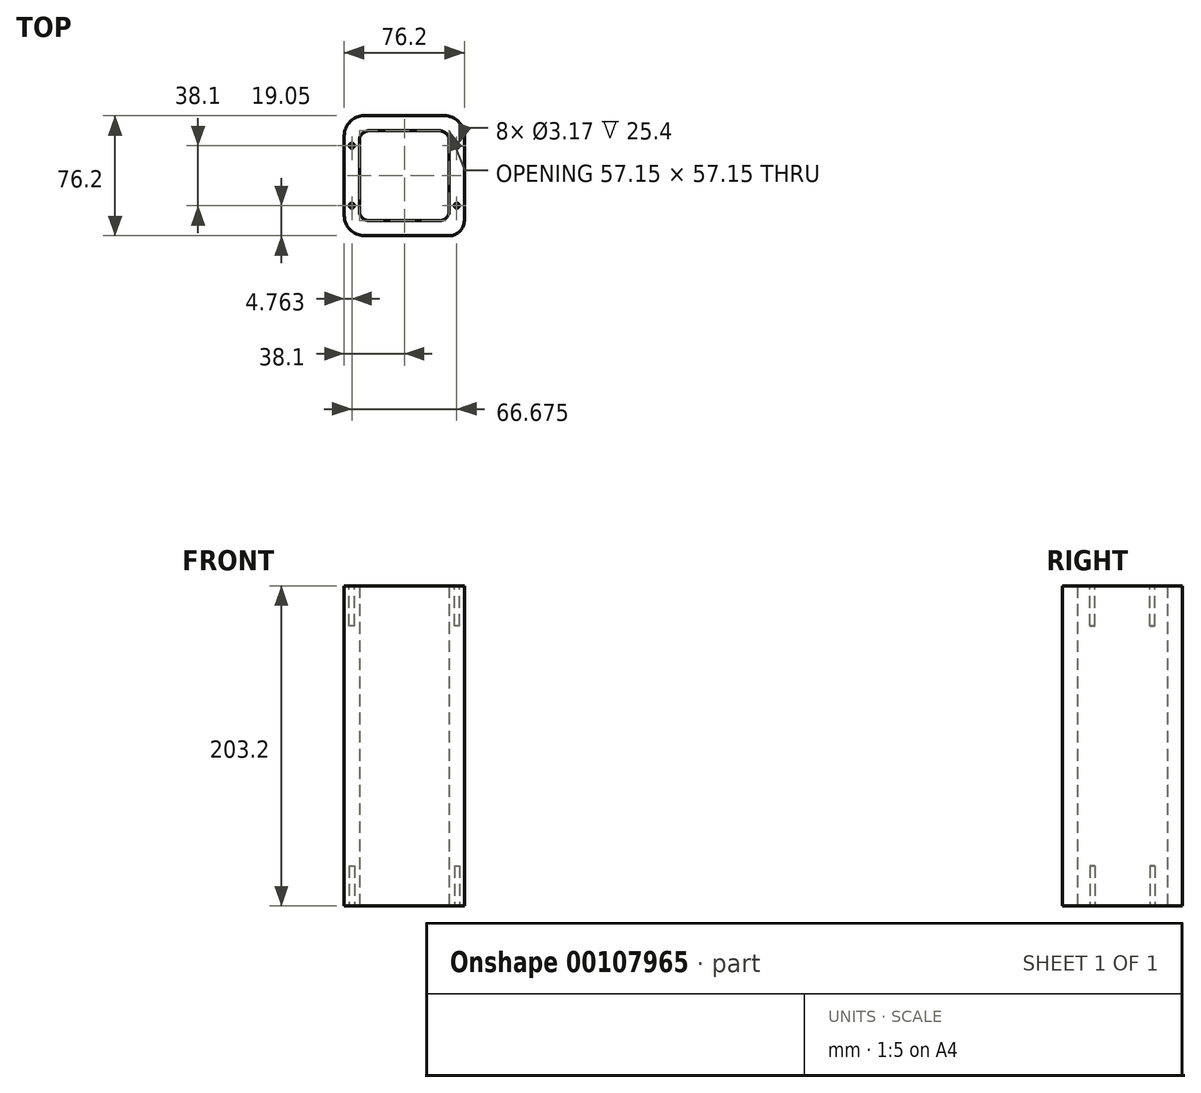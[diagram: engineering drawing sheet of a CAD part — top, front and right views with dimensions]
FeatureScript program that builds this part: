
annotation { "Feature Type Name" : "Feature", "Feature Type Description" : "" }
export const myFeature = defineFeature(function(context is Context, id is Id, definition is map)
    precondition{}
    {
        {
            var Q0;
            Q0=qCreatedBy(makeId("Top.planeOp"),FACE);
            var sketch = newSketch(context, id + "F0", { "sketchPlane" : qUnion([Q0])});
            skLineSegment(sketch, "E0.bottom", {"start": v(28.57, -38.1) * mm, "end": v(-25.4, -38.1) * mm});
            skLineSegment(sketch, "E0.top", {"start": v(25.4, 38.1) * mm, "end": v(-25.4, 38.1) * mm});
            skLineSegment(sketch, "E0.left", {"start": v(38.1, -28.58) * mm, "end": v(38.1, 25.4) * mm});
            skLineSegment(sketch, "E0.right", {"start": v(-38.1, -25.4) * mm, "end": v(-38.1, 25.4) * mm});
            skPoint(sketch, "E0.middle", {"position": v(0, 0) * mm});
            skPoint(sketch, "E1.visualSharp", {"position": v(-38.1, 38.1) * mm});
            skArc(sketch, "E1.filletArc", {"start": v(-25.4, 38.1) * mm, "mid": v(-34.38, 34.38) * mm, "end": v(-38.1, 25.4) * mm});
            skPoint(sketch, "E2.visualSharp", {"position": v(38.1, 38.1) * mm});
            skArc(sketch, "E2.filletArc", {"start": v(38.1, 25.4) * mm, "mid": v(34.38, 34.38) * mm, "end": v(25.4, 38.1) * mm});
            skPoint(sketch, "E3.visualSharp", {"position": v(38.1, -38.1) * mm});
            skArc(sketch, "E3.filletArc", {"start": v(28.58, -38.1) * mm, "mid": v(35.31, -35.31) * mm, "end": v(38.1, -28.58) * mm});
            skPoint(sketch, "E4.visualSharp", {"position": v(-38.1, -38.1) * mm});
            skArc(sketch, "E4.filletArc", {"start": v(-38.1, -25.4) * mm, "mid": v(-34.38, -34.38) * mm, "end": v(-25.4, -38.1) * mm});
            skLineSegment(sketch, "E5.bottom", {"start": v(22.23, -28.58) * mm, "end": v(-22.23, -28.58) * mm});
            skLineSegment(sketch, "E5.top", {"start": v(22.23, 28.58) * mm, "end": v(-22.23, 28.58) * mm});
            skLineSegment(sketch, "E5.left", {"start": v(28.58, -22.23) * mm, "end": v(28.58, 22.23) * mm});
            skLineSegment(sketch, "E5.right", {"start": v(-28.58, -22.23) * mm, "end": v(-28.58, 22.23) * mm});
            skPoint(sketch, "E6.visualSharp", {"position": v(-28.58, 28.58) * mm});
            skArc(sketch, "E6.filletArc", {"start": v(-22.23, 28.58) * mm, "mid": v(-26.72, 26.72) * mm, "end": v(-28.58, 22.23) * mm});
            skPoint(sketch, "E7.visualSharp", {"position": v(28.58, 28.58) * mm});
            skArc(sketch, "E7.filletArc", {"start": v(28.58, 22.23) * mm, "mid": v(26.72, 26.72) * mm, "end": v(22.23, 28.58) * mm});
            skArc(sketch, "E8.filletArc", {"start": v(22.23, -28.58) * mm, "mid": v(26.72, -26.72) * mm, "end": v(28.58, -22.23) * mm});
            skPoint(sketch, "E9.visualSharp", {"position": v(-28.58, -28.58) * mm});
            skArc(sketch, "E9.filletArc", {"start": v(-28.58, -22.23) * mm, "mid": v(-26.72, -26.72) * mm, "end": v(-22.23, -28.58) * mm});
            skSolve(sketch);
        }
        {
            var Q0;
            Q0=makeQuery(id+"F0.imprint","IMPRINT",FACE,{"disambiguationData":[TD([[makeQuery(id+"F0.imprint","IMPRINT",EDGE,{"derivedFrom":sQuery(id+"F0.wireOp",EDGE,"E0.bottom")}),-1.0]])]});
            extrude(context, id + "F1", {"entities" : qUnion([Q0]), "depth" : 203.2 * mm});
        }
        {
            var Q0;
            Q0=makeQuery(id+"F1.opExtrude","CAP_FACE",FACE,{"disambiguationData":[OSD([sQuery(id+"F0.wireOp",EDGE,"E0.bottom"),sQuery(id+"F0.wireOp",EDGE,"E0.top"),sQuery(id+"F0.wireOp",EDGE,"E0.left"),sQuery(id+"F0.wireOp",EDGE,"E0.right"),sQuery(id+"F0.wireOp",EDGE,"E1.filletArc"),sQuery(id+"F0.wireOp",EDGE,"E2.filletArc"),sQuery(id+"F0.wireOp",EDGE,"E3.filletArc"),sQuery(id+"F0.wireOp",EDGE,"E4.filletArc"),sQuery(id+"F0.wireOp",EDGE,"E5.bottom"),sQuery(id+"F0.wireOp",EDGE,"E5.top"),sQuery(id+"F0.wireOp",EDGE,"E5.left"),sQuery(id+"F0.wireOp",EDGE,"E5.right"),sQuery(id+"F0.wireOp",EDGE,"E6.filletArc"),sQuery(id+"F0.wireOp",EDGE,"E7.filletArc"),sQuery(id+"F0.wireOp",EDGE,"E8.filletArc"),sQuery(id+"F0.wireOp",EDGE,"E9.filletArc")])],"isStart":false});
            var sketch = newSketch(context, id + "F2", { "sketchPlane" : qUnion([Q0])});
            skLineSegment(sketch, "E10.bottom", {"start": v(33.34, -33.34) * mm, "end": v(-33.34, -33.34) * mm, "construction": true});
            skLineSegment(sketch, "E10.top", {"start": v(33.34, 33.34) * mm, "end": v(-33.34, 33.34) * mm, "construction": true});
            skLineSegment(sketch, "E10.left", {"start": v(33.34, -33.34) * mm, "end": v(33.34, 33.34) * mm, "construction": true});
            skLineSegment(sketch, "E10.right", {"start": v(-33.34, -33.34) * mm, "end": v(-33.34, 33.34) * mm, "construction": true});
            skPoint(sketch, "E10.middle", {"position": v(0, 0) * mm});
            skLineSegment(sketch, "E11", {"start": v(-49.5, 19.05) * mm, "end": v(53.9, 19.05) * mm, "construction": true});
            skLineSegment(sketch, "E12", {"start": v(49.19, -19.05) * mm, "end": v(-54.56, -19.05) * mm, "construction": true});
            skCircle(sketch, "E13", {"center": v(-33.34, 19.05) * mm, "radius": 1.59 * mm});
            skCircle(sketch, "E14", {"center": v(-33.34, -19.05) * mm, "radius": 1.59 * mm});
            skCircle(sketch, "E15", {"center": v(33.34, 19.05) * mm, "radius": 1.59 * mm});
            skCircle(sketch, "E16", {"center": v(33.34, -19.05) * mm, "radius": 1.59 * mm});
            skSolve(sketch);
        }
        {
            var Q0;
            Q0=makeQuery(id+"F2.imprint","IMPRINT",FACE,{"disambiguationData":[TD([[makeQuery(id+"F2.imprint","IMPRINT",EDGE,{"derivedFrom":sQuery(id+"F2.wireOp",EDGE,"E13")}),1.0]])]});
            var Q1;
            Q1=makeQuery(id+"F2.imprint","IMPRINT",FACE,{"disambiguationData":[TD([[makeQuery(id+"F2.imprint","IMPRINT",EDGE,{"derivedFrom":sQuery(id+"F2.wireOp",EDGE,"E14")}),1.0]])]});
            var Q2;
            Q2=makeQuery(id+"F2.imprint","IMPRINT",FACE,{"disambiguationData":[TD([[makeQuery(id+"F2.imprint","IMPRINT",EDGE,{"derivedFrom":sQuery(id+"F2.wireOp",EDGE,"E16")}),1.0]])]});
            var Q3;
            Q3=makeQuery(id+"F2.imprint","IMPRINT",FACE,{"disambiguationData":[TD([[makeQuery(id+"F2.imprint","IMPRINT",EDGE,{"derivedFrom":sQuery(id+"F2.wireOp",EDGE,"E15")}),1.0]])]});
            extrude(context, id + "F3", {"entities" : qUnion([Q0, Q1, Q2, Q3]), "operationType" : NewBodyOperationType.REMOVE, "oppositeDirection" : true, "depth" : 25.4 * mm});
        }
        {
            var Q0;
            Q0=makeQuery(id+"F1.opExtrude","CAP_FACE",FACE,{"disambiguationData":[OSD([sQuery(id+"F0.wireOp",EDGE,"E0.bottom"),sQuery(id+"F0.wireOp",EDGE,"E0.top"),sQuery(id+"F0.wireOp",EDGE,"E0.left"),sQuery(id+"F0.wireOp",EDGE,"E0.right"),sQuery(id+"F0.wireOp",EDGE,"E1.filletArc"),sQuery(id+"F0.wireOp",EDGE,"E2.filletArc"),sQuery(id+"F0.wireOp",EDGE,"E3.filletArc"),sQuery(id+"F0.wireOp",EDGE,"E4.filletArc"),sQuery(id+"F0.wireOp",EDGE,"E5.bottom"),sQuery(id+"F0.wireOp",EDGE,"E5.top"),sQuery(id+"F0.wireOp",EDGE,"E5.left"),sQuery(id+"F0.wireOp",EDGE,"E5.right"),sQuery(id+"F0.wireOp",EDGE,"E6.filletArc"),sQuery(id+"F0.wireOp",EDGE,"E7.filletArc"),sQuery(id+"F0.wireOp",EDGE,"E8.filletArc"),sQuery(id+"F0.wireOp",EDGE,"E9.filletArc")])],"isStart":true});
            var sketch = newSketch(context, id + "F4", { "sketchPlane" : qUnion([Q0])});
            skLineSegment(sketch, "E17.bottom", {"start": v(33.34, -33.34) * mm, "end": v(-33.34, -33.34) * mm, "construction": true});
            skLineSegment(sketch, "E17.top", {"start": v(33.34, 33.34) * mm, "end": v(-33.34, 33.34) * mm, "construction": true});
            skLineSegment(sketch, "E17.left", {"start": v(33.34, -33.34) * mm, "end": v(33.34, 33.34) * mm, "construction": true});
            skLineSegment(sketch, "E17.right", {"start": v(-33.34, -33.34) * mm, "end": v(-33.34, 33.34) * mm, "construction": true});
            skPoint(sketch, "E17.middle", {"position": v(0, 0) * mm});
            skLineSegment(sketch, "E18", {"start": v(-46.97, 19.05) * mm, "end": v(56.62, 19.05) * mm, "construction": true});
            skLineSegment(sketch, "E19", {"start": v(-44.75, -19.05) * mm, "end": v(54.53, -19.05) * mm, "construction": true});
            skCircle(sketch, "E20", {"center": v(-33.34, 19.05) * mm, "radius": 1.59 * mm});
            skCircle(sketch, "E21", {"center": v(-33.34, -19.05) * mm, "radius": 1.59 * mm});
            skCircle(sketch, "E22", {"center": v(33.34, 19.05) * mm, "radius": 1.59 * mm});
            skCircle(sketch, "E23", {"center": v(33.34, -19.05) * mm, "radius": 1.59 * mm});
            skSolve(sketch);
        }
        {
            var Q0;
            Q0=makeQuery(id+"F4.imprint","IMPRINT",FACE,{"disambiguationData":[TD([[makeQuery(id+"F4.imprint","IMPRINT",EDGE,{"derivedFrom":sQuery(id+"F4.wireOp",EDGE,"E20")}),1.0]])]});
            var Q1;
            Q1=makeQuery(id+"F4.imprint","IMPRINT",FACE,{"disambiguationData":[TD([[makeQuery(id+"F4.imprint","IMPRINT",EDGE,{"derivedFrom":sQuery(id+"F4.wireOp",EDGE,"E21")}),1.0]])]});
            var Q2;
            Q2=makeQuery(id+"F4.imprint","IMPRINT",FACE,{"disambiguationData":[TD([[makeQuery(id+"F4.imprint","IMPRINT",EDGE,{"derivedFrom":sQuery(id+"F4.wireOp",EDGE,"E22")}),1.0]])]});
            var Q3;
            Q3=makeQuery(id+"F4.imprint","IMPRINT",FACE,{"disambiguationData":[TD([[makeQuery(id+"F4.imprint","IMPRINT",EDGE,{"derivedFrom":sQuery(id+"F4.wireOp",EDGE,"E23")}),1.0]])]});
            extrude(context, id + "F5", {"entities" : qUnion([Q0, Q1, Q2, Q3]), "operationType" : NewBodyOperationType.REMOVE, "oppositeDirection" : true, "depth" : 25.4 * mm});
        }
    });
